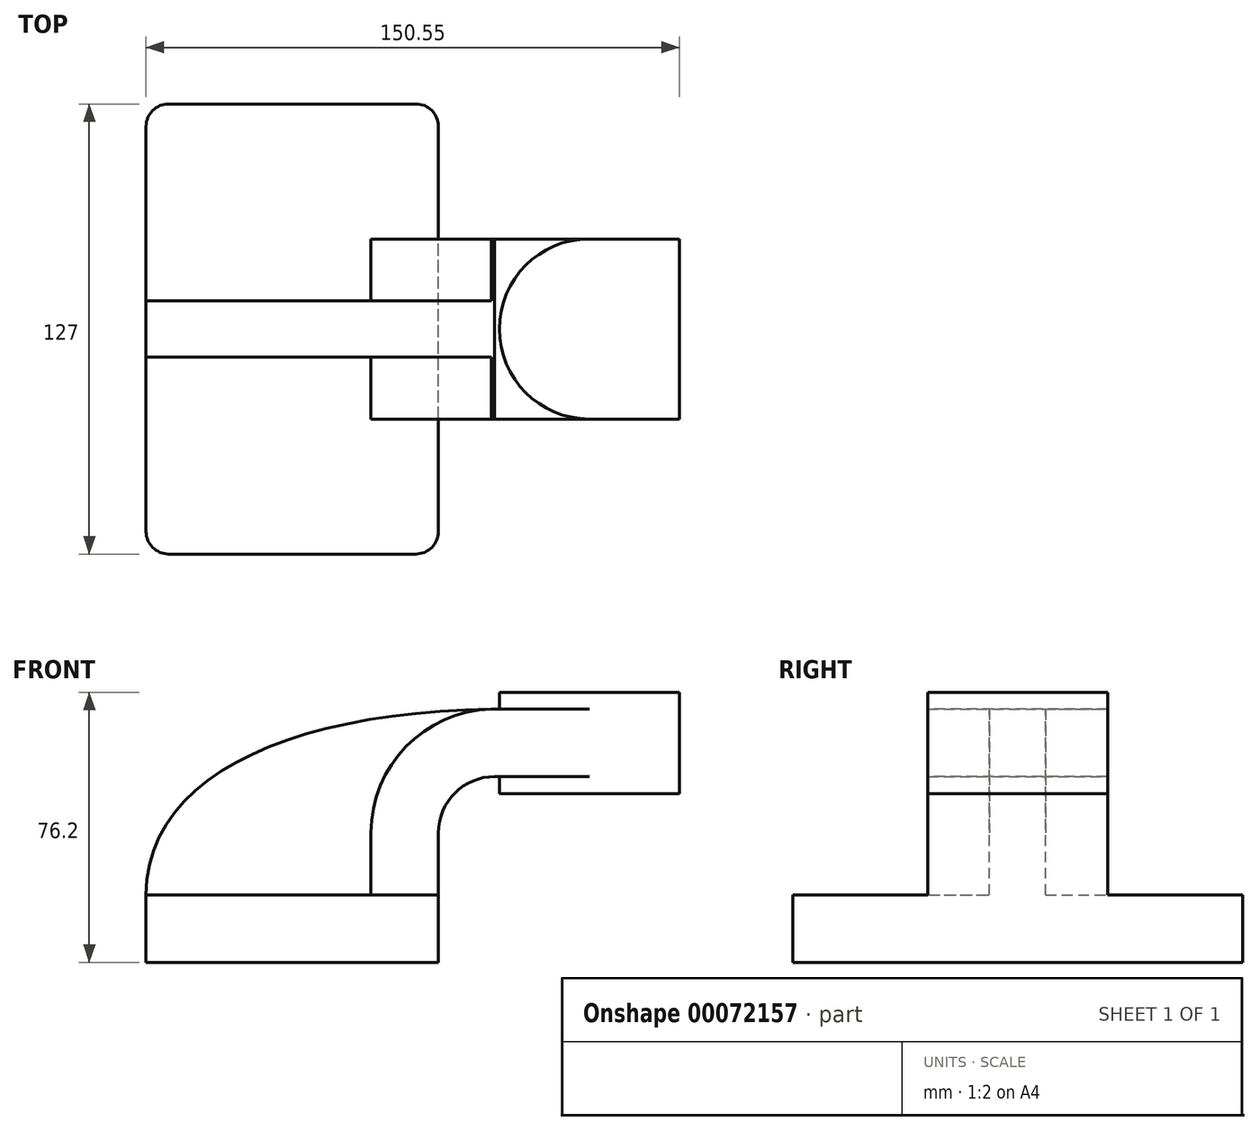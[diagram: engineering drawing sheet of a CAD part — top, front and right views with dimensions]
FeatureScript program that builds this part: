
annotation { "Feature Type Name" : "Feature", "Feature Type Description" : "" }
export const myFeature = defineFeature(function(context is Context, id is Id, definition is map)
    precondition{}
    {
        {
            var Q0;
            Q0=qCreatedBy(makeId("Front.planeOp"),FACE);
            var sketch = newSketch(context, id + "F0", { "sketchPlane" : qUnion([Q0])});
            skLineSegment(sketch, "E0.rect.bottom", {"start": v(-41.28, 9.52) * mm, "end": v(41.28, 9.53) * mm});
            skLineSegment(sketch, "E0.rect.top", {"start": v(-41.28, -9.53) * mm, "end": v(41.28, -9.53) * mm});
            skLineSegment(sketch, "E0.rect.left", {"start": v(-41.28, 9.52) * mm, "end": v(-41.28, -9.53) * mm});
            skLineSegment(sketch, "E0.rect.right", {"start": v(41.28, 9.53) * mm, "end": v(41.28, -9.52) * mm});
            skPoint(sketch, "E0.rect.middle", {"position": v(0, 0) * mm});
            skLineSegment(sketch, "E1.rect.bottom", {"start": v(109.27, 66.68) * mm, "end": v(58.47, 66.68) * mm});
            skLineSegment(sketch, "E1.rect.top", {"start": v(109.27, 38.1) * mm, "end": v(58.47, 38.1) * mm});
            skLineSegment(sketch, "E1.rect.left", {"start": v(109.27, 66.68) * mm, "end": v(109.27, 38.1) * mm});
            skLineSegment(sketch, "E1.rect.right", {"start": v(58.47, 66.68) * mm, "end": v(58.47, 38.1) * mm});
            skPoint(sketch, "E1.rect.middle", {"position": v(83.87, 52.39) * mm});
            skLineSegment(sketch, "E2", {"start": v(41.27, 9.53) * mm, "end": v(41.27, 27) * mm});
            skArc(sketch, "E3", {"start": v(41.27, 27) * mm, "mid": v(45.92, 38.23) * mm, "end": v(57.15, 42.88) * mm});
            skLineSegment(sketch, "E4", {"start": v(57.15, 42.88) * mm, "end": v(85.72, 42.88) * mm});
            skLineSegment(sketch, "E5.0", {"start": v(22.22, 9.53) * mm, "end": v(22.22, 27) * mm});
            skArc(sketch, "E6.0", {"start": v(22.22, 27) * mm, "mid": v(32.45, 51.7) * mm, "end": v(57.15, 61.93) * mm});
            skLineSegment(sketch, "E7", {"start": v(83.87, 38.1) * mm, "end": v(83.87, 66.68) * mm});
            skLineSegment(sketch, "E8", {"start": v(57.15, 61.93) * mm, "end": v(83.87, 61.93) * mm});
            skFitSpline(sketch, "E9", {"points": [v(-41.28, 9.52) * mm, v(57.15, 61.93) * mm], "startDerivative": vector(0.84, 101.76) * mm, "endDerivative": vector(171.45, 2.13) * mm});
            skSolve(sketch);
        }
        {
            var Q0;
            Q0=makeQuery(id+"F0.imprint","IMPRINT",FACE,{"disambiguationData":[TD([[makeQuery(id+"F0.imprint","IMPRINT",EDGE,{"derivedFrom":sQuery(id+"F0.wireOp",EDGE,"E0.rect.top")}),1.0]])]});
            extrude(context, id + "F1", {"entities" : qUnion([Q0]), "depth" : 127 * mm, "symmetric" : true});
        }
        {
            var Q0;
            {var subQ5=sQuery(id+"F0.wireOp",EDGE,"E2");Q0=makeQuery(id+"F0.imprint","IMPRINT",FACE,{"disambiguationData":[TD([[makeQuery(id+"F0.imprint","IMPRINT",EDGE,{"derivedFrom":subQ5}),1.0]])]});}
            var Q1;
            {var subQ0=sQuery(id+"F0.wireOp",EDGE,"E8");var subQ1=sQuery(id+"F0.wireOp",EDGE,"E1.rect.right");var subQ2=makeQuery(id+"F0.imprint","INTERSECT",VERTEX,{"derivedFrom":[subQ1,subQ0]});Q1=makeQuery(id+"F0.imprint","IMPRINT",FACE,{"disambiguationData":[TD([[makeQuery(id+"F0.imprint","IMPRINT",EDGE,{"disambiguationData":[TD([[subQ2,-1.0]])],"derivedFrom":subQ1}),1.0]])]});}
            var Q2;
            {var subQ0=sQuery(id+"F0.wireOp",EDGE,"E1.rect.left");Q2=makeQuery(id+"F0.imprint","IMPRINT",FACE,{"disambiguationData":[TD([[makeQuery(id+"F0.imprint","IMPRINT",EDGE,{"derivedFrom":subQ0}),-1.0]])]});}
            extrude(context, id + "F2", {"entities" : qUnion([Q0, Q1, Q2]), "operationType" : NewBodyOperationType.ADD, "depth" : 50.8 * mm, "symmetric" : true});
        }
        {
            var Q0;
            {var subQ3=sQuery(id+"F0.wireOp",EDGE,"E5.0");Q0=makeQuery(id+"F0.imprint","IMPRINT",FACE,{"disambiguationData":[TD([[makeQuery(id+"F0.imprint","IMPRINT",EDGE,{"derivedFrom":subQ3}),1.0]])]});}
            extrude(context, id + "F3", {"entities" : qUnion([Q0]), "operationType" : NewBodyOperationType.ADD, "depth" : 15.88 * mm, "symmetric" : true});
        }
        {
            var Q0;
            {var subQ0=sQuery(id+"F0.wireOp",EDGE,"E1.rect.left");Q0=makeQuery(id+"F0.imprint","IMPRINT",FACE,{"disambiguationData":[TD([[makeQuery(id+"F0.imprint","IMPRINT",EDGE,{"derivedFrom":subQ0}),-1.0]])]});}
            var Q1;
            Q1=sQuery(id+"F0.wireOp",EDGE,"E7");
            revolve(context, id + "F4", {"operationType" : NewBodyOperationType.ADD, "entities" : qUnion([Q0]), "axis" : qUnion([Q1]), "revolveType" : RevolveType.FULL});
        }
        {
            var Q0;
            Q0=makeQuery(id+"F1.opExtrude","CAP_EDGE",EDGE,{"disambiguationData":[OSD([sQuery(id+"F0.wireOp",EDGE,"E0.rect.left")])],"isStart":true});
            var Q1;
            Q1=makeQuery(id+"F1.opExtrude","CAP_EDGE",EDGE,{"disambiguationData":[OSD([sQuery(id+"F0.wireOp",EDGE,"E0.rect.left")])],"isStart":false});
            var Q2;
            Q2=makeQuery(id+"F1.opExtrude","CAP_EDGE",EDGE,{"disambiguationData":[OSD([sQuery(id+"F0.wireOp",EDGE,"E0.rect.right")])],"isStart":false});
            var Q3;
            Q3=makeQuery(id+"F1.opExtrude","CAP_EDGE",EDGE,{"disambiguationData":[OSD([sQuery(id+"F0.wireOp",EDGE,"E0.rect.right")])],"isStart":true});
            fillet(context, id + "F5", {"entities" : qUnion([Q0, Q1, Q2, Q3]), "radius" : 6.35 * mm, "tangentPropagation" : true, "allowEdgeOverflow" : false});
        }
    });
